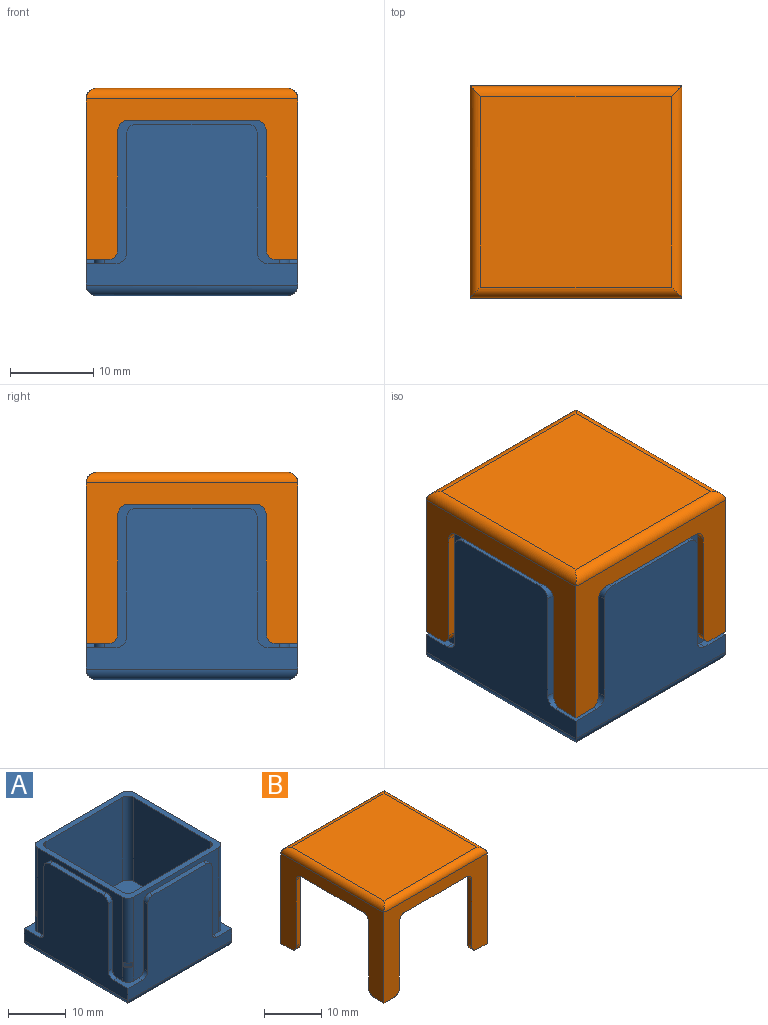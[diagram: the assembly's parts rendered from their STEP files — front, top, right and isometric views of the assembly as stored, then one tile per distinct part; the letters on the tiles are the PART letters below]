
ASSEMBLY  parts=2 mates=1
PART A: 71 faces, bbox 25.4x25.4x21.6 mm
  f0: plane 20.96x17.78mm, normal (1,0,0), area 108.6mm2, adj f8,f11,f13,f24,f25,f26,f34,f37
  f1: plane 20.96x17.78mm, normal (0,1,0), area 108.6mm2, adj f8,f10,f11,f18,f19,f20,f31,f37
  f2: plane 20.96x17.78mm, normal (-1,0,0), area 108.6mm2, adj f8,f10,f12,f27,f28,f29,f31,f36
  f3: plane 20.96x17.78mm, normal (0,-1,0), area 108.6mm2, adj f8,f12,f13,f21,f22,f23,f34,f36
  f4: plane 18.8x17.78mm, normal (0,-1,0), area 334.2mm2, adj f8,f9,f32,f38
  f5: plane 18.8x17.78mm, normal (-1,0,0), area 334.2mm2, adj f8,f9,f33,f38
  f6: plane 18.8x17.78mm, normal (0,1,0), area 334.2mm2, adj f8,f9,f33,f35
  f7: plane 18.8x17.78mm, normal (1,0,0), area 334.2mm2, adj f8,f9,f32,f35
  f8: plane 23.5x23.5mm, normal (0,0,1), area 96.8mm2, adj f0,f1,f2,f3,f4,f5,f6,f7
  f9: plane 21.34x21.34mm, normal (0,0,1), area 453.8mm2, adj f4,f5,f6,f7,f32,f33,f35,f38
  f10: plane 3.56x3.56mm, normal (0,0,1), area 6.2mm2, adj f1,f2,f14,f17,f31,f40,f45
  f11: plane 3.56x3.56mm, normal (0,0,1), area 6.2mm2, adj f0,f1,f16,f17,f37,f41,f46
  f12: plane 3.56x3.56mm, normal (0,0,1), area 6.2mm2, adj f2,f3,f14,f15,f36,f39,f43
  f13: plane 3.56x3.56mm, normal (0,0,1), area 6.2mm2, adj f0,f3,f15,f16,f34,f42,f44
  f14: plane 25.4x19.3mm, normal (-1,0,0), area 328.5mm2, adj f10,f12,f15,f17,f27,f28,f29,f39
  f15: plane 25.4x19.3mm, normal (0,-1,0), area 328.5mm2, adj f12,f13,f14,f16,f21,f22,f23,f43
  f16: plane 25.4x19.3mm, normal (1,0,0), area 328.5mm2, adj f11,f13,f15,f17,f24,f25,f26,f41
  f17: plane 25.4x19.3mm, normal (0,1,0), area 328.5mm2, adj f10,f11,f14,f16,f18,f19,f20,f45
  f18: plane 14.22x0.95mm, normal (-1,0,0), area 13.5mm2, adj f1,f17,f45,f54
  f19: plane 14.22x0.95mm, normal (1,0,0), area 13.5mm2, adj f1,f17,f46,f53
  f20: plane 13.21x0.95mm, normal (0,0,1), area 12.6mm2, adj f1,f17,f53,f54
  f21: plane 14.22x0.95mm, normal (-1,0,0), area 13.5mm2, adj f3,f15,f43,f50
  f22: plane 14.22x0.95mm, normal (1,0,0), area 13.5mm2, adj f3,f15,f44,f49
  f23: plane 13.21x0.95mm, normal (0,0,1), area 12.6mm2, adj f3,f15,f49,f50
  f24: plane 14.22x0.95mm, normal (0,1,0), area 13.5mm2, adj f0,f16,f41,f48
  f25: plane 14.22x0.95mm, normal (0,-1,0), area 13.5mm2, adj f0,f16,f42,f47
  f26: plane 13.21x0.95mm, normal (0,0,1), area 12.6mm2, adj f0,f16,f47,f48
  f27: plane 14.22x0.95mm, normal (0,-1,0), area 13.5mm2, adj f2,f14,f39,f51
  f28: plane 14.22x0.95mm, normal (0,1,0), area 13.5mm2, adj f2,f14,f40,f52
  f29: plane 13.21x0.95mm, normal (0,0,1), area 12.6mm2, adj f2,f14,f51,f52
  f30: plane 22.86x22.86mm, normal (0,0,-1), area 522.6mm2, adj f55,f56,f57,f58
  f31: cylinder r=1.27mm len=17.78mm, axis (0,0,-1), area 33.7mm2, adj f1,f2,f8,f10,f68,f69,f70
  f32: cylinder r=1.27mm len=17.78mm, axis (0,0,1), area 35.5mm2, adj f4,f7,f8,f9
  f33: cylinder r=1.27mm len=17.78mm, axis (0,0,1), area 35.5mm2, adj f5,f6,f8,f9
  f34: cylinder r=1.27mm len=17.78mm, axis (0,0,-1), area 33.7mm2, adj f0,f3,f8,f13,f65,f66,f67
  f35: cylinder r=1.27mm len=17.78mm, axis (0,0,-1), area 35.5mm2, adj f6,f7,f8,f9
  f36: cylinder r=1.27mm len=17.78mm, axis (0,0,1), area 33.7mm2, adj f2,f3,f8,f12,f62,f63,f64
  f37: cylinder r=1.27mm len=17.78mm, axis (0,0,1), area 33.7mm2, adj f0,f1,f8,f11,f59,f60,f61
  f38: cylinder r=1.27mm len=17.78mm, axis (0,0,-1), area 35.5mm2, adj f4,f5,f8,f9
  f39: cylinder r=1.27mm len=1.27mm, axis (-1,0,0), area 1.9mm2, adj f2,f12,f14,f27
  f40: cylinder r=1.27mm len=1.27mm, axis (1,0,0), area 1.9mm2, adj f2,f10,f14,f28
  f41: cylinder r=1.27mm len=1.27mm, axis (1,0,0), area 1.9mm2, adj f0,f11,f16,f24
  f42: cylinder r=1.27mm len=1.27mm, axis (-1,0,0), area 1.9mm2, adj f0,f13,f16,f25
  f43: cylinder r=1.27mm len=1.27mm, axis (0,1,0), area 1.9mm2, adj f3,f12,f15,f21
  f44: cylinder r=1.27mm len=1.27mm, axis (0,-1,0), area 1.9mm2, adj f3,f13,f15,f22
  f45: cylinder r=1.27mm len=1.27mm, axis (0,1,0), area 1.9mm2, adj f1,f10,f17,f18
  f46: cylinder r=1.27mm len=1.27mm, axis (0,-1,0), area 1.9mm2, adj f1,f11,f17,f19
  f47: cylinder r=1.27mm len=1.27mm, axis (-1,0,0), area 1.9mm2, adj f0,f16,f25,f26
  f48: cylinder r=1.27mm len=1.27mm, axis (1,0,0), area 1.9mm2, adj f0,f16,f24,f26
  f49: cylinder r=1.27mm len=1.27mm, axis (0,-1,0), area 1.9mm2, adj f3,f15,f22,f23
  f50: cylinder r=1.27mm len=1.27mm, axis (0,1,0), area 1.9mm2, adj f3,f15,f21,f23
  f51: cylinder r=1.27mm len=1.27mm, axis (-1,0,0), area 1.9mm2, adj f2,f14,f27,f29
  f52: cylinder r=1.27mm len=1.27mm, axis (1,0,0), area 1.9mm2, adj f2,f14,f28,f29
  f53: cylinder r=1.27mm len=1.27mm, axis (0,-1,0), area 1.9mm2, adj f1,f17,f19,f20
  f54: cylinder r=1.27mm len=1.27mm, axis (0,1,0), area 1.9mm2, adj f1,f17,f18,f20
  f55: cylinder r=1.27mm len=25.4mm, axis (1,0,0), area 48.8mm2, adj f15,f30,f56,f57
  f56: cylinder r=1.27mm len=25.4mm, axis (0,1,0), area 48.8mm2, adj f16,f30,f55,f58
  f57: cylinder r=1.27mm len=25.4mm, axis (0,-1,0), area 48.8mm2, adj f14,f30,f55,f58
  f58: cylinder r=1.27mm len=25.4mm, axis (-1,0,0), area 48.8mm2, adj f17,f30,f56,f57
  f59: plane 1.13x1.13mm, normal (0.71,0.71,0), area 1.6mm2, adj f37,f60,f61
  f60: plane 1.13x1.13mm, normal (0,0,-1), area 0.3mm2, adj f37,f59
  f61: plane 1.13x1.13mm, normal (0,0,1), area 0.3mm2, adj f37,f59
  f62: plane 1.13x1.13mm, normal (-0.71,-0.71,0), area 1.6mm2, adj f36,f63,f64
  f63: plane 1.13x1.13mm, normal (0,0,-1), area 0.3mm2, adj f36,f62
  f64: plane 1.13x1.13mm, normal (0,0,1), area 0.3mm2, adj f36,f62
  f65: plane 1.13x1.13mm, normal (0.71,-0.71,0), area 1.6mm2, adj f34,f66,f67
  f66: plane 1.13x1.13mm, normal (0,0,-1), area 0.3mm2, adj f34,f65
  f67: plane 1.13x1.13mm, normal (0,0,1), area 0.3mm2, adj f34,f65
  f68: plane 1.13x1.13mm, normal (-0.71,0.71,0), area 1.6mm2, adj f31,f69,f70
  f69: plane 1.13x1.13mm, normal (0,0,-1), area 0.3mm2, adj f31,f68
  f70: plane 1.13x1.13mm, normal (0,0,1), area 0.3mm2, adj f31,f68
PART B: 58 faces, bbox 25.4x25.4x20.6 mm
  f0: plane 25.4x25.4mm, normal (0,0,-1), area 610.1mm2, adj f1,f2,f3,f4,f8,f9,f13,f14
  f1: plane 25.4x19.3mm, normal (0,-1,0), area 192.3mm2, adj f0,f2,f4,f19,f20,f21,f25,f27
  f2: plane 25.4x19.3mm, normal (1,0,0), area 192.3mm2, adj f0,f1,f3,f6,f10,f16,f20,f26
  f3: plane 25.4x19.3mm, normal (0,1,0), area 192.3mm2, adj f0,f2,f4,f7,f10,f11,f15,f31
  f4: plane 25.4x19.3mm, normal (-1,0,0), area 192.3mm2, adj f0,f1,f3,f12,f15,f24,f25,f28
  f5: plane 22.86x22.86mm, normal (0,0,1), area 522.6mm2, adj f34,f35,f36,f37
  f6: plane 14.22x0.95mm, normal (0,-1,0), area 13.5mm2, adj f2,f9,f33,f45
  f7: plane 14.22x0.95mm, normal (-1,0,0), area 13.5mm2, adj f3,f8,f32,f44
  f8: plane 16.76x4.13mm, normal (0,-1,0), area 47.6mm2, adj f0,f7,f9,f10,f32,f44,f46,f47
  f9: plane 16.76x4.13mm, normal (-1,0,0), area 47.6mm2, adj f0,f6,f8,f10,f33,f45,f46,f47
  f10: plane 2.54x2.54mm, normal (0,0,-1), area 3.9mm2, adj f2,f3,f8,f9,f44,f45
  f11: plane 14.22x0.95mm, normal (1,0,0), area 13.5mm2, adj f3,f14,f31,f43
  f12: plane 14.22x0.95mm, normal (0,-1,0), area 13.5mm2, adj f4,f13,f30,f42
  f13: plane 16.76x4.13mm, normal (1,0,0), area 47.6mm2, adj f0,f12,f14,f15,f30,f42,f49,f50
  f14: plane 16.76x4.13mm, normal (0,-1,0), area 47.6mm2, adj f0,f11,f13,f15,f31,f43,f49,f50
  f15: plane 2.54x2.54mm, normal (0,0,-1), area 3.9mm2, adj f3,f4,f13,f14,f42,f43
  f16: plane 14.22x0.95mm, normal (0,1,0), area 13.5mm2, adj f2,f17,f26,f38
  f17: plane 16.76x4.13mm, normal (-1,0,0), area 47.6mm2, adj f0,f16,f18,f20,f26,f38,f52,f53
  f18: plane 16.76x4.13mm, normal (0,1,0), area 47.6mm2, adj f0,f17,f19,f20,f27,f39,f52,f53
  f19: plane 14.22x0.95mm, normal (-1,0,0), area 13.5mm2, adj f1,f18,f27,f39
  f20: plane 2.54x2.54mm, normal (0,0,-1), area 3.9mm2, adj f1,f2,f17,f18,f38,f39
  f21: plane 14.22x0.95mm, normal (1,0,0), area 13.5mm2, adj f1,f22,f29,f41
  f22: plane 16.76x4.13mm, normal (0,1,0), area 47.6mm2, adj f0,f21,f23,f25,f29,f41,f55,f56
  f23: plane 16.76x4.13mm, normal (1,0,0), area 47.6mm2, adj f0,f22,f24,f25,f28,f40,f55,f56
  f24: plane 14.22x0.95mm, normal (0,1,0), area 13.5mm2, adj f4,f23,f28,f40
  f25: plane 2.54x2.54mm, normal (0,0,-1), area 3.9mm2, adj f1,f4,f22,f23,f40,f41
  f26: cylinder r=1.27mm len=1.27mm, axis (-1,0,0), area 1.9mm2, adj f0,f2,f16,f17
  f27: cylinder r=1.27mm len=1.27mm, axis (0,-1,0), area 1.9mm2, adj f0,f1,f18,f19
  f28: cylinder r=1.27mm len=1.27mm, axis (-1,0,0), area 1.9mm2, adj f0,f4,f23,f24
  f29: cylinder r=1.27mm len=1.27mm, axis (0,1,0), area 1.9mm2, adj f0,f1,f21,f22
  f30: cylinder r=1.27mm len=1.27mm, axis (1,0,0), area 1.9mm2, adj f0,f4,f12,f13
  f31: cylinder r=1.27mm len=1.27mm, axis (0,1,0), area 1.9mm2, adj f0,f3,f11,f14
  f32: cylinder r=1.27mm len=1.27mm, axis (0,-1,0), area 1.9mm2, adj f0,f3,f7,f8
  f33: cylinder r=1.27mm len=1.27mm, axis (1,0,0), area 1.9mm2, adj f0,f2,f6,f9
  f34: cylinder r=1.27mm len=25.4mm, axis (0,1,0), area 48.8mm2, adj f4,f5,f35,f36
  f35: cylinder r=1.27mm len=25.4mm, axis (1,0,0), area 48.8mm2, adj f3,f5,f34,f37
  f36: cylinder r=1.27mm len=25.4mm, axis (-1,0,0), area 48.8mm2, adj f1,f5,f34,f37
  f37: cylinder r=1.27mm len=25.4mm, axis (0,-1,0), area 48.8mm2, adj f2,f5,f35,f36
  f38: cylinder r=1.27mm len=1.27mm, axis (1,0,0), area 1.9mm2, adj f2,f16,f17,f20
  f39: cylinder r=1.27mm len=1.27mm, axis (0,1,0), area 1.9mm2, adj f1,f18,f19,f20
  f40: cylinder r=1.27mm len=1.27mm, axis (1,0,0), area 1.9mm2, adj f4,f23,f24,f25
  f41: cylinder r=1.27mm len=1.27mm, axis (0,-1,0), area 1.9mm2, adj f1,f21,f22,f25
  f42: cylinder r=1.27mm len=1.27mm, axis (-1,0,0), area 1.9mm2, adj f4,f12,f13,f15
  f43: cylinder r=1.27mm len=1.27mm, axis (0,-1,0), area 1.9mm2, adj f3,f11,f14,f15
  f44: cylinder r=1.27mm len=1.27mm, axis (0,1,0), area 1.9mm2, adj f3,f7,f8,f10
  f45: cylinder r=1.27mm len=1.27mm, axis (-1,0,0), area 1.9mm2, adj f2,f6,f9,f10
  f46: plane 0.64x0.64mm, normal (-0.71,-0.71,0), area 0.5mm2, adj f8,f9,f47,f48
  f47: plane 0.64x0.64mm, normal (0,0,1), area 0.2mm2, adj f8,f9,f46
  f48: plane 0.64x0.64mm, normal (0,0,-1), area 0.2mm2, adj f8,f9,f46
  f49: plane 0.64x0.64mm, normal (0.71,-0.71,0), area 0.5mm2, adj f13,f14,f50,f51
  f50: plane 0.64x0.64mm, normal (0,0,1), area 0.2mm2, adj f13,f14,f49
  f51: plane 0.64x0.64mm, normal (0,0,-1), area 0.2mm2, adj f13,f14,f49
  f52: plane 0.64x0.64mm, normal (-0.71,0.71,0), area 0.5mm2, adj f17,f18,f53,f54
  f53: plane 0.64x0.64mm, normal (0,0,1), area 0.2mm2, adj f17,f18,f52
  f54: plane 0.64x0.64mm, normal (0,0,-1), area 0.2mm2, adj f17,f18,f52
  f55: plane 0.64x0.64mm, normal (0.71,0.71,0), area 0.5mm2, adj f22,f23,f56,f57
  f56: plane 0.64x0.64mm, normal (0,0,1), area 0.2mm2, adj f22,f23,f55
  f57: plane 0.64x0.64mm, normal (0,0,-1), area 0.2mm2, adj f22,f23,f55
PLACE A t=(-5.41,1.06,-4.53)mm fixed
PLACE B t=(-5.41,1.06,-5.08)mm
MATE slider B.f20 <-> A.f13  axis (0,0,-1) through (7.29,-11.64,-0.25)mm
